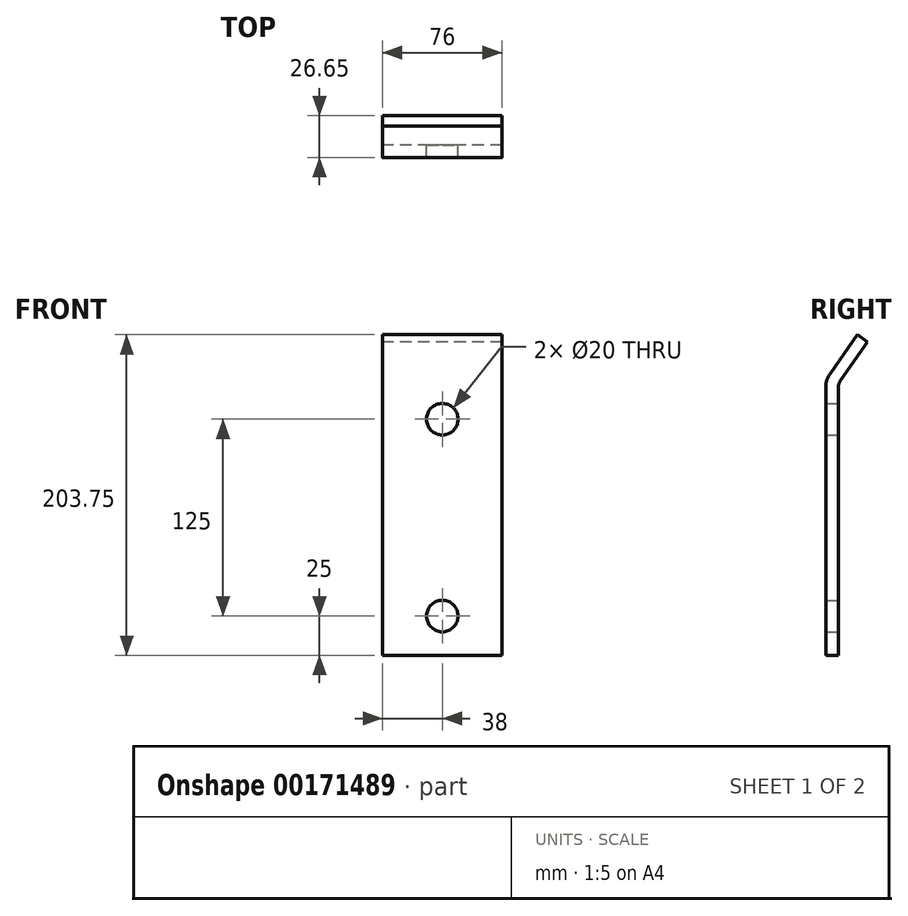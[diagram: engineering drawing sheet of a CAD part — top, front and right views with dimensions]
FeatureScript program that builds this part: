
annotation { "Feature Type Name" : "Feature", "Feature Type Description" : "" }
export const myFeature = defineFeature(function(context is Context, id is Id, definition is map)
    precondition{}
    {
        {
            var Q0;
            Q0=qCreatedBy(makeId("Right.planeOp"),FACE);
            var sketch = newSketch(context, id + "F0", { "sketchPlane" : qUnion([Q0])});
            skLineSegment(sketch, "E0", {"start": v(0, 0) * mm, "end": v(0, 170) * mm});
            skLineSegment(sketch, "E1", {"start": v(2.9, 179.18) * mm, "end": v(20.1, 203.75) * mm});
            skLineSegment(sketch, "E2", {"start": v(20.1, 203.75) * mm, "end": v(26.65, 199.16) * mm});
            skLineSegment(sketch, "E3", {"start": v(26.65, 199.16) * mm, "end": v(9.45, 174.59) * mm});
            skLineSegment(sketch, "E4", {"start": v(8, 170) * mm, "end": v(8, 0) * mm});
            skLineSegment(sketch, "E5", {"start": v(8, 0) * mm, "end": v(0, 0) * mm});
            skPoint(sketch, "E6.visualSharp", {"position": v(8, 172.52) * mm});
            skArc(sketch, "E6.filletArc", {"start": v(9.45, 174.59) * mm, "mid": v(8.37, 172.4) * mm, "end": v(8, 170) * mm});
            skPoint(sketch, "E7.visualSharp", {"position": v(0, 175.04) * mm});
            skArc(sketch, "E7.filletArc", {"start": v(2.9, 179.18) * mm, "mid": v(0.74, 174.81) * mm, "end": v(0, 170) * mm});
            skSolve(sketch);
        }
        {
            var Q0;
            Q0=makeQuery(id+"F0.imprint","IMPRINT",FACE,{"disambiguationData":[TD([[makeQuery(id+"F0.imprint","IMPRINT",EDGE,{"derivedFrom":sQuery(id+"F0.wireOp",EDGE,"E0")}),-1.0]])]});
            extrude(context, id + "F1", {"entities" : qUnion([Q0]), "depth" : 76 * mm});
        }
        {
            var Q0;
            Q0=makeQuery(id+"F1.opExtrude","SWEPT_FACE",FACE,{"disambiguationData":[OSD([sQuery(id+"F0.wireOp",EDGE,"E4")])]});
            var sketch = newSketch(context, id + "F2", { "sketchPlane" : qUnion([Q0])});
            skLineSegment(sketch, "E8", {"start": v(-38, 0) * mm, "end": v(-38, 25) * mm, "construction": true});
            skLineSegment(sketch, "E9", {"start": v(-38, 25) * mm, "end": v(-38, 150) * mm, "construction": true});
            skCircle(sketch, "E10", {"center": v(-38, 25) * mm, "radius": 10 * mm});
            skCircle(sketch, "E11", {"center": v(-38, 150) * mm, "radius": 10 * mm});
            skSolve(sketch);
        }
        {
            var Q0;
            Q0=makeQuery(id+"F2.imprint","IMPRINT",FACE,{"disambiguationData":[TD([[makeQuery(id+"F2.imprint","IMPRINT",EDGE,{"derivedFrom":sQuery(id+"F2.wireOp",EDGE,"E11")}),1.0]])]});
            var Q1;
            Q1=makeQuery(id+"F2.imprint","IMPRINT",FACE,{"disambiguationData":[TD([[makeQuery(id+"F2.imprint","IMPRINT",EDGE,{"derivedFrom":sQuery(id+"F2.wireOp",EDGE,"E10")}),1.0]])]});
            extrude(context, id + "F3", {"entities" : qUnion([Q0, Q1]), "operationType" : NewBodyOperationType.REMOVE, "endBound" : BoundingType.THROUGH_ALL, "oppositeDirection" : true, "depth" : 25 * mm});
        }
    });
